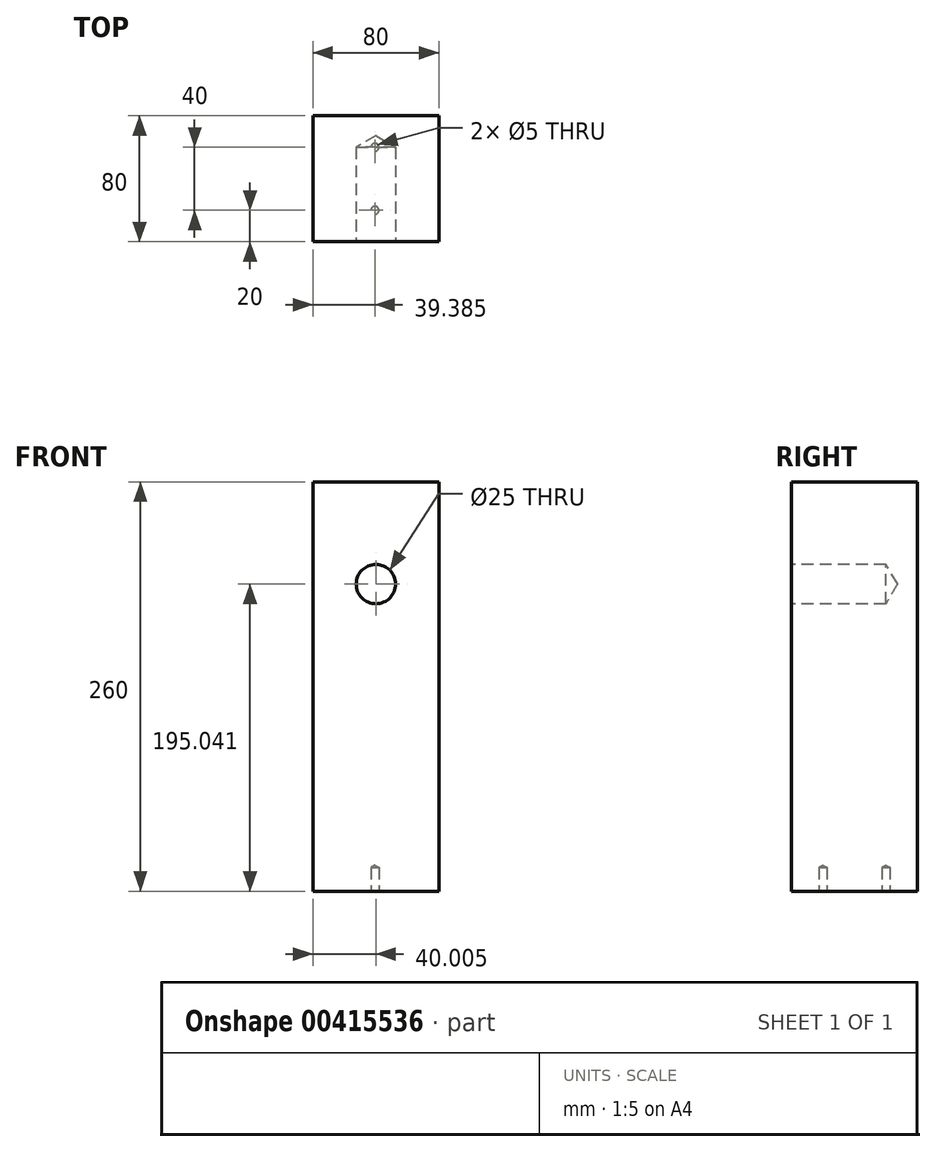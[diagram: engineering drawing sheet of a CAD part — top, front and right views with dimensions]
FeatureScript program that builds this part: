
annotation { "Feature Type Name" : "Feature", "Feature Type Description" : "" }
export const myFeature = defineFeature(function(context is Context, id is Id, definition is map)
    precondition{}
    {
        {
            var Q0;
            Q0=qCreatedBy(makeId("Top.planeOp"),FACE);
            var sketch = newSketch(context, id + "F0", { "sketchPlane" : qUnion([Q0])});
            skLineSegment(sketch, "E0.bottom", {"start": v(0, 0) * mm, "end": v(80, 0) * mm});
            skLineSegment(sketch, "E0.top", {"start": v(0, 80) * mm, "end": v(80, 80) * mm});
            skLineSegment(sketch, "E0.left", {"start": v(0, 0) * mm, "end": v(0, 80) * mm});
            skLineSegment(sketch, "E0.right", {"start": v(80, 0) * mm, "end": v(80, 80) * mm});
            skSolve(sketch);
        }
        {
            var Q0;
            Q0 = qSketchRegion(id + "F0", true);
            extrude(context, id + "F1", {"entities" : qUnion([Q0]), "depth" : 260 * mm});
        }
        {
            var Q0;
            Q0=makeQuery(id+"F1.opExtrude","SWEPT_FACE",FACE,{"disambiguationData":[OSD([sQuery(id+"F0.wireOp",EDGE,"E0.bottom")])]});
            var sketch = newSketch(context, id + "F2", { "sketchPlane" : qUnion([Q0])});
            skLineSegment(sketch, "E1", {"start": v(40, 195) * mm, "end": v(40, 195.04) * mm});
            skCircle(sketch, "E2", {"center": v(40, 195.04) * mm, "radius": 0.04 * mm});
            skCircle(sketch, "E3", {"center": v(40, 195) * mm, "radius": 12.5 * mm});
            skSolve(sketch);
        }
        {
            var Q0;
            Q0=sQuery(id+"F2.wireOp",VERTEX,"E2.center");
            var Q1;
            Q1=makeQuery(id+"F1.opExtrude","SWEPT_BODY",BODY,{"disambiguationData":[OSD([sQuery(id+"F0.wireOp",EDGE,"E0.bottom"),sQuery(id+"F0.wireOp",EDGE,"E0.top"),sQuery(id+"F0.wireOp",EDGE,"E0.left"),sQuery(id+"F0.wireOp",EDGE,"E0.right")])]});
            hole(context, id + "F3", {"style" : HoleStyle.SIMPLE, "endStyle" : HoleEndStyle.BLIND, "holeDiameter" : 25 * mm, "holeDepth" : 60 * mm, "isTappedThrough" : true, "tappedDepth" : 12.7 * mm, "tapClearance" : 3, "locations" : qUnion([Q0]), "scope" : qUnion([Q1])});
        }
        {
            var Q0;
            Q0=makeQuery(id+"F1.opExtrude","CAP_FACE",FACE,{"disambiguationData":[OSD([sQuery(id+"F0.wireOp",EDGE,"E0.bottom"),sQuery(id+"F0.wireOp",EDGE,"E0.top"),sQuery(id+"F0.wireOp",EDGE,"E0.left"),sQuery(id+"F0.wireOp",EDGE,"E0.right")])],"isStart":true});
            var sketch = newSketch(context, id + "F4", { "sketchPlane" : qUnion([Q0])});
            skPoint(sketch, "E4", {"position": v(39.38, -20) * mm});
            skPoint(sketch, "E5", {"position": v(39.38, -60) * mm});
            skLineSegment(sketch, "E6", {"start": v(39.38, -20) * mm, "end": v(39.38, -60) * mm});
            skSolve(sketch);
        }
        {
            var Q0;
            Q0=sQuery(id+"F4.wireOp",VERTEX,"E6.start");
            var Q1;
            Q1=sQuery(id+"F4.wireOp",VERTEX,"E6.end");
            var Q2;
            Q2=makeQuery(id+"F1.opExtrude","SWEPT_BODY",BODY,{"disambiguationData":[OSD([sQuery(id+"F0.wireOp",EDGE,"E0.bottom"),sQuery(id+"F0.wireOp",EDGE,"E0.top"),sQuery(id+"F0.wireOp",EDGE,"E0.left"),sQuery(id+"F0.wireOp",EDGE,"E0.right")])]});
            hole(context, id + "F5", {"style" : HoleStyle.SIMPLE, "endStyle" : HoleEndStyle.BLIND, "holeDiameter" : 5 * mm, "holeDepth" : 15 * mm, "isTappedThrough" : true, "tappedDepth" : 12.7 * mm, "tapClearance" : 3, "locations" : qUnion([Q0, Q1]), "scope" : qUnion([Q2])});
        }
    });
